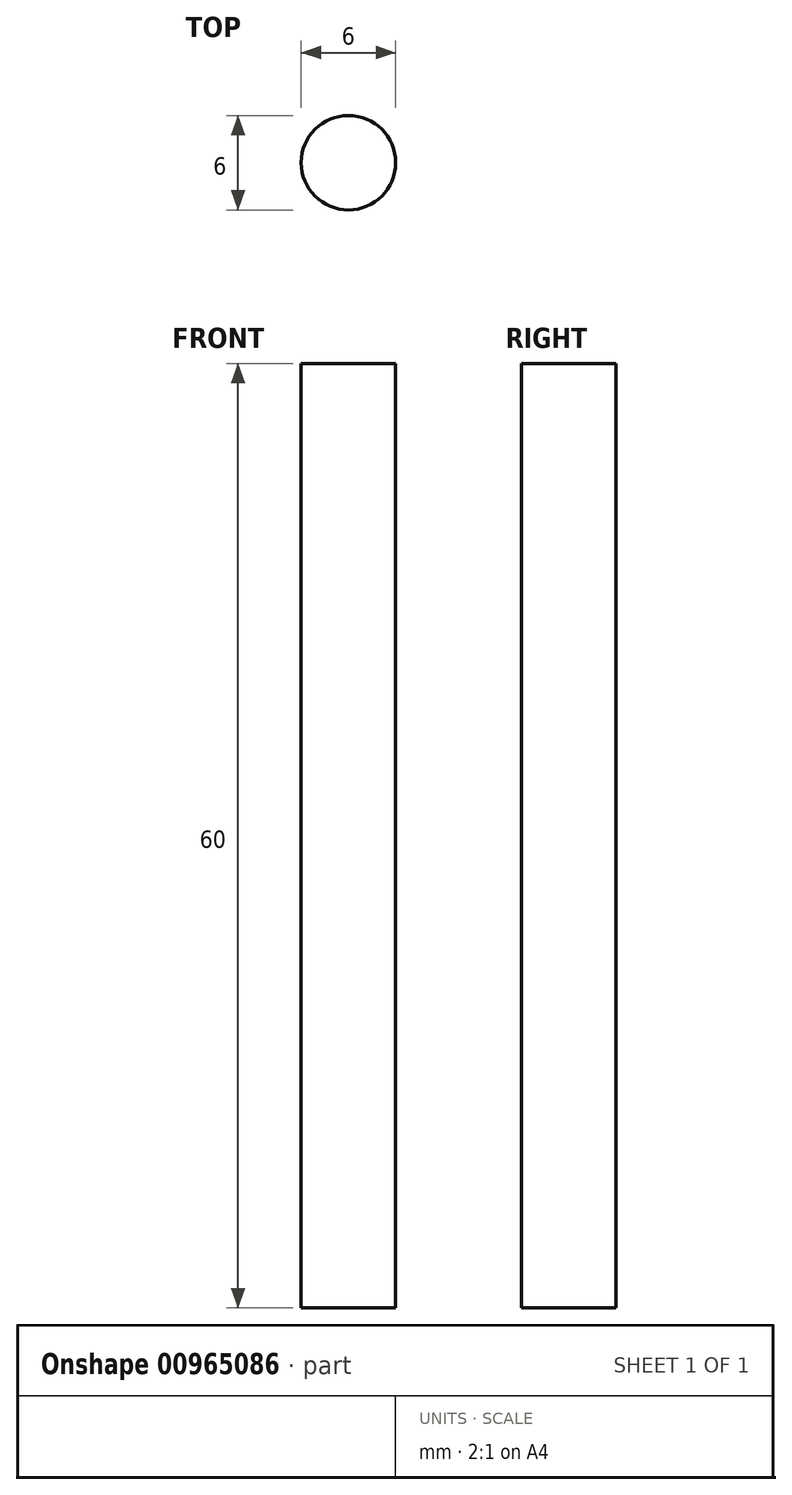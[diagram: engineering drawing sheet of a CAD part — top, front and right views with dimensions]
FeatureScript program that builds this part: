
annotation { "Feature Type Name" : "Feature", "Feature Type Description" : "" }
export const myFeature = defineFeature(function(context is Context, id is Id, definition is map)
    precondition{}
    {
        {
            var Q0;
            Q0=qCreatedBy(makeId("Top.planeOp"),FACE);
            var sketch = newSketch(context, id + "F0", { "sketchPlane" : qUnion([Q0])});
            skCircle(sketch, "E0", {"center": v(0, 0) * mm, "radius": 3 * mm});
            skSolve(sketch);
        }
        {
            var Q0;
            Q0=makeQuery(id+"F0.imprint","IMPRINT",FACE,{"disambiguationData":[TD([[makeQuery(id+"F0.imprint","IMPRINT",EDGE,{"derivedFrom":sQuery(id+"F0.wireOp",EDGE,"E0")}),1.0]])]});
            extrude(context, id + "F1", {"entities" : qUnion([Q0]), "depth" : 60 * mm, "offsetDistance" : 25 * mm});
        }
    });
